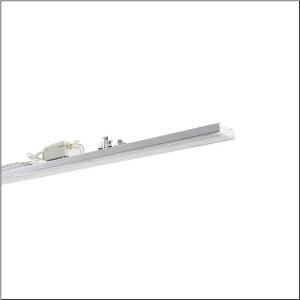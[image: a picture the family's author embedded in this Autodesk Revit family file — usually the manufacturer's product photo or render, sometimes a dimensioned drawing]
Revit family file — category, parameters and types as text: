
# Revit family: licross_21_recessed_ho_52tl1ede47xs
name_source: partatom
category: Lighting Fixtures
units: mm (PartAtom-declared; Revit-internal decimal feet)

## family parameters
Cut with Voids When Loaded = No
Host = Face
Light Source = No
Part Type = Normal
Room Calculation Point = No
Round Connector Dimension = Use Diameter
Shared = No

## types (1)
- --- (1 x LED, 7310 lm, 44.1 W, 4000K)
    Apparent Load = 44 VA
    CIE Flux Codes = 85 95 99 100 100
    Color Rendering = 80
    Color Temperature = 4000K
    Default Elevation = 1800 mm
    Description = Licross 21 Recessed HO, luminaire insert, of sheet steel, galvanised, coil coated, white, length: 750mm, width: 66mm, height: 67mm, LED rated luminous flux: 7.310lm, light colour: 840, SDCM (Standard Deviation of Colour Matching)MacAdam ≤ 3 SDCM (initial), control gear: DALI 2, with plug, 5-pole, with phase selection, mains connection: 220..240V, AC, 50/60Hz, rated input power: 44W, internal wiring halogen-free, primary light control with lens, of plastic, primary optical cover: cover, of PMMA, light emission: direct distribution, primary light characteristic: symmetric, protection rating (complete): IP40, insulation class (complete): insulation class I (protective earthing), certification: CE, ENEC, VDE, UKCA, protection symbol: D if used in an environment without relevant dust loads with corresponding accessories, impact resistance: IK06, permissible ambient temperature for indoor applications: -25..+30°C, corresponds to IFS (International Featured Standards) requirements for safety and quality in the food industry, reducing of maximum allowable ambient temperature of 5°C with ceiling mounting, LABS conformity tested according to VDMA 24364:2018-05, The light source and the operating device comply with the requirements of the Ecodesign Regulation (EU) 2019/2020 and are replaceable in accordance with this regulation, packaging unit: 1 piece
    Height = 58 mm
    Lamp = 1 x LED
    Lamp Light Flux = 7310 lm
    Lamp Power = 44.1 W
    Lamp count = 1
    Length = 750 mm
    Luminous efficacy = 166 lm/W
    Manufacturer = Siteco
    ModVariant = No
    Model = 52TL1EDE47XS
    Mounting Place = Ceiling
    Mounting Type = Pendant
    Number of Poles = 1
    OnlyDefault = Yes
    Power Factor = 1
    Product Name = Licross 21 Recessed HO
    Product group = luminaire insert | ceiling pendant
    ProductGroupID = 901
    Protection Class = Protection class I
    Protection Degree = IP 40
    RLX_Detail_Level = 1
    RLX_Emergency_Light_Flux = 0 lm
    RLX_Emergency_Type = 0
    RLX_Emergency_Type_DB = No
    RlxData = <blob elided: 29689 chars, md5=5bc35eae>
    Socket = socket
    Standby Power = 0 W
    System Light Flux = 7310 lm
    System Power = 44 W
    Type Comments = factory setting: luminous flux: 100 % | dim-lin: 254 | 484 mA
    Type Image = l_1296930.jpg
    URL = http://relux.com
    VarID = @adj_127355
    Voltage = 0 V
    Weight = 0.00 kg
    Width = 66 mm

## geometry (parser evidence)
native form markers: Blend x4, Sweep x8
no freeform markers — native parametric forms only
